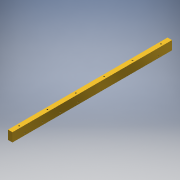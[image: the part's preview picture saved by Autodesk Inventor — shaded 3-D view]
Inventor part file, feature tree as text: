
AUTODESK INVENTOR PART (.ipt)
format: ipt  version: 2017 (Build 210142000, 142)  size: 135,680 bytes
history: native  units: in
note: dims shown in document units (in); Inventor stores cm internally (conversion verified against a paired STEP export)
features: sketch x3, hole x3, pattern_linear x2, extrude x1
ambient origin geometry x8: Origin, YZ Plane, XZ Plane, XY Plane, X Axis, Y Axis, Z Axis, Center Point
bodies: Solid1 (feature_tree)
feature tree (9):
  extrude  "Extrusion1"  Depth=0.5in
  sketch  "Sketch3"  dims[d6=9.0in d7=0.0in d8=0.3703in]
  hole  "Hole1"  [1 undecoded]
  pattern_linear  "Rectangular Pattern1"  Count1=4 Spacing1=1.0in
  hole  "Hole5"  [1 undecoded]
  hole  "Hole6"  [1 undecoded]
  pattern_linear  "Rectangular Pattern5"  Spacing1=0.5in  [1 undecoded]
  sketch  "Sketch2"  dims[d3=0.25in d5=0.5in]
  sketch  "Sketch7"  dims[d9=0.7in d10=0.067in d11=0.75in d12=0.375in d13=0.25in d14=0.5635in d15=1.0in d16=0.8108in d17=1.5748in d19=1.0in d60=8.2in d61=0.3703in d62=0.067in d63=0.75in d64=0.375in d65=0.25in d66=0.5635in d67=1.0in d68=0.8108in d69=0.5in d70=0.125in d71=0.067in d72=0.75in d73=0.375in d74=0.25in d75=0.5635in d76=0.25in d77=0.8108in d78=2.3622in d80=1.6in]
note: 4 required parameter values undecoded (feature->parameter linkage not recoverable at this tier; creation-order binding heuristic only, values carry confidence <= 0.55)
